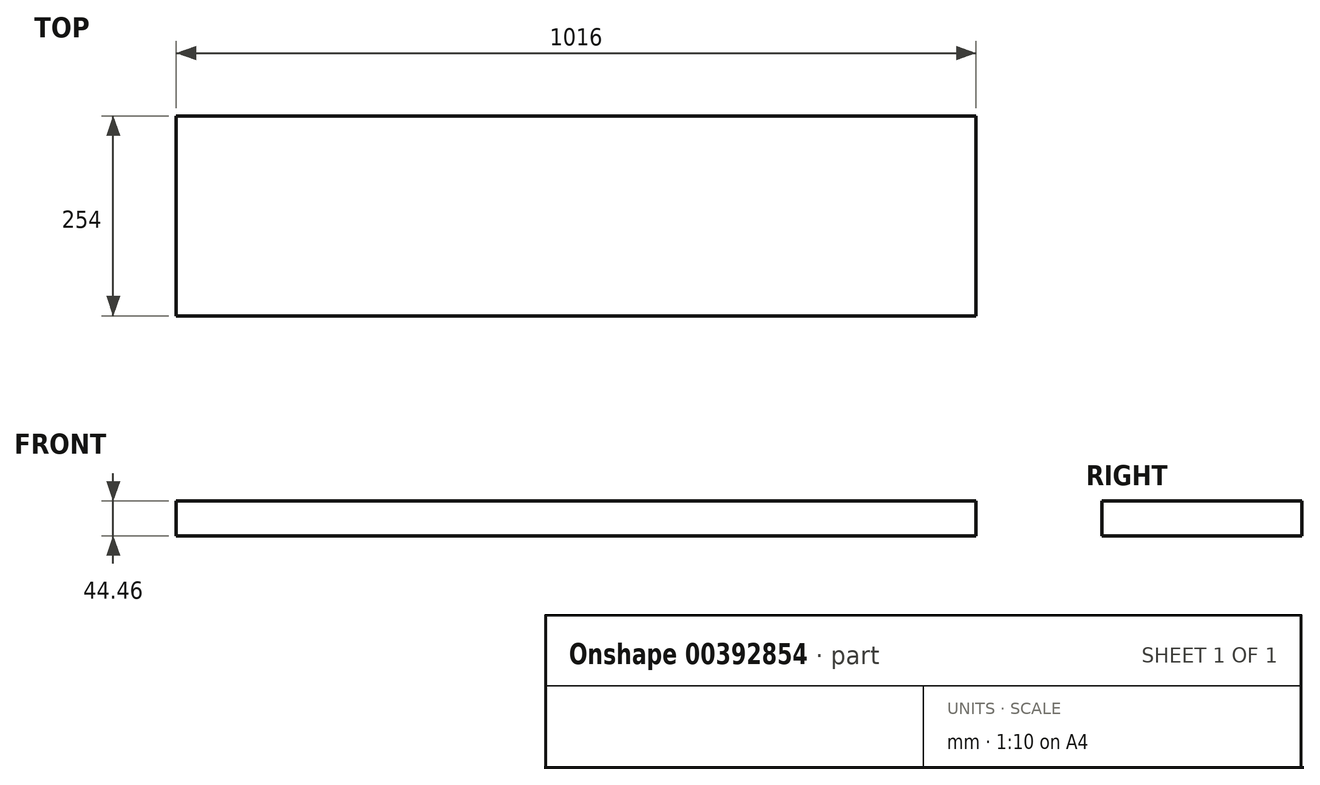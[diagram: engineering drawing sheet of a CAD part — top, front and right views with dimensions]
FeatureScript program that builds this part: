
annotation { "Feature Type Name" : "Feature", "Feature Type Description" : "" }
export const myFeature = defineFeature(function(context is Context, id is Id, definition is map)
    precondition{}
    {
        {
            var Q0;
            Q0=qCreatedBy(makeId("Right.planeOp"),FACE);
            var sketch = newSketch(context, id + "F0", { "sketchPlane" : qUnion([Q0])});
            skLineSegment(sketch, "E0.bottom", {"start": v(-127, -22.22) * mm, "end": v(127, -22.22) * mm});
            skLineSegment(sketch, "E0.top", {"start": v(-127, 22.22) * mm, "end": v(127, 22.22) * mm});
            skLineSegment(sketch, "E0.left", {"start": v(-127, -22.22) * mm, "end": v(-127, 22.22) * mm});
            skLineSegment(sketch, "E0.right", {"start": v(127, -22.22) * mm, "end": v(127, 22.22) * mm});
            skPoint(sketch, "E0.middle", {"position": v(0, 0) * mm});
            skSolve(sketch);
        }
        {
            var Q0;
            Q0 = qSketchRegion(id + "F0", true);
            extrude(context, id + "F1", {"entities" : qUnion([Q0]), "depth" : 1016 * mm, "symmetric" : true});
        }
    });
